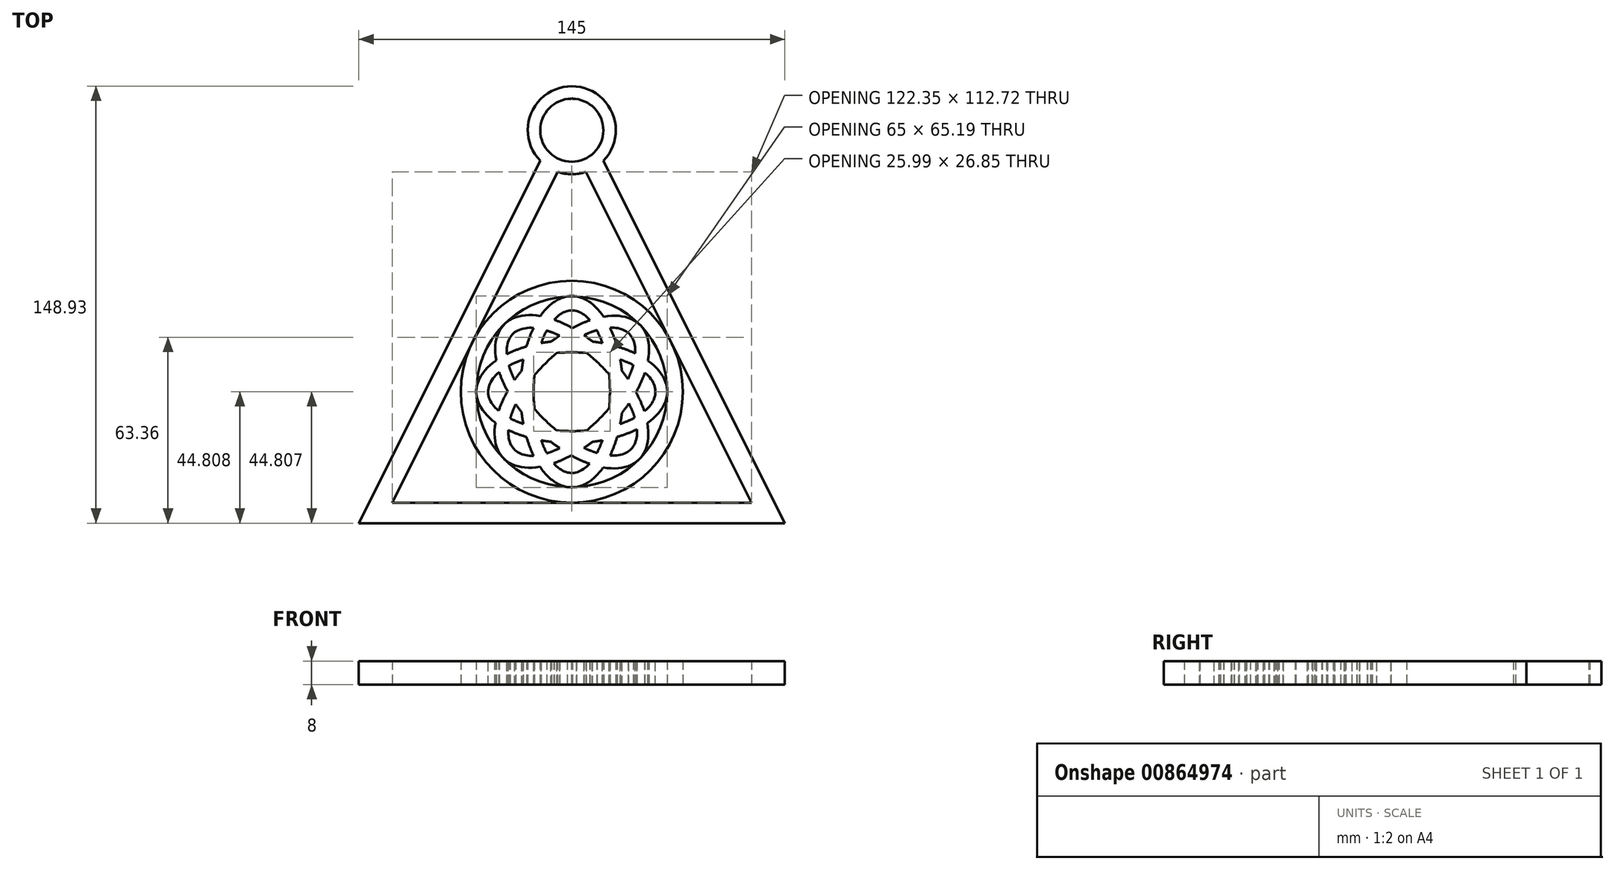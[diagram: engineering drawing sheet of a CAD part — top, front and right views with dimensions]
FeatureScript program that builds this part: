
annotation { "Feature Type Name" : "Feature", "Feature Type Description" : "" }
export const myFeature = defineFeature(function(context is Context, id is Id, definition is map)
    precondition{}
    {
        {
            var Q0;
            Q0=qCreatedBy(makeId("Top.planeOp"),FACE);
            var sketch = newSketch(context, id + "F0", { "sketchPlane" : qUnion([Q0])});
            skLineSegment(sketch, "E0.bottom", {"start": v(72.5, -72.5) * mm, "end": v(-72.5, -72.5) * mm});
            skPoint(sketch, "E0.middle", {"position": v(0, 0) * mm});
            skLineSegment(sketch, "E1", {"start": v(0, 72.5) * mm, "end": v(-0.16, 72.18) * mm});
            skLineSegment(sketch, "E2", {"start": v(0, 72.5) * mm, "end": v(0.16, 72.18) * mm});
            skCircle(sketch, "E3", {"center": v(0, 61.43) * mm, "radius": 10.75 * mm});
            skLineSegment(sketch, "E4", {"start": v(-4.81, 47.22) * mm, "end": v(-61.17, -65.5) * mm});
            skLineSegment(sketch, "E5", {"start": v(4.81, 47.22) * mm, "end": v(61.17, -65.5) * mm});
            skLineSegment(sketch, "E6", {"start": v(-61.17, -65.5) * mm, "end": v(61.17, -65.5) * mm});
            skArc(sketch, "E7", {"start": v(-4.81, 47.22) * mm, "mid": v(0, 46.43) * mm, "end": v(4.81, 47.22) * mm});
            skLineSegment(sketch, "E8.trimOffspring", {"start": v(-10.76, 50.98) * mm, "end": v(-72.5, -72.5) * mm});
            skLineSegment(sketch, "E9.trimOffspring", {"start": v(10.76, 50.98) * mm, "end": v(72.5, -72.5) * mm});
            skArc(sketch, "E10.trimOffspring", {"start": v(10.76, 50.98) * mm, "mid": v(0, 76.43) * mm, "end": v(-10.76, 50.98) * mm});
            skCircle(sketch, "E11", {"center": v(0, -27.7) * mm, "radius": 37.8 * mm});
            skCircle(sketch, "E12", {"center": v(0, -27.7) * mm, "radius": 32.5 * mm});
            skPoint(sketch, "E0.right.end.orphan", {"position": v(-72.5, 72.5) * mm});
            skPoint(sketch, "E0.left.end.orphan", {"position": v(72.5, 72.5) * mm});
            skLineSegment(sketch, "E13", {"start": v(22.98, -4.72) * mm, "end": v(22.98, -4.71) * mm});
            skLineSegment(sketch, "E14", {"start": v(0, -27.7) * mm, "end": v(0, -27.7) * mm});
            skEllipticalArc(sketch, "E15", {});
            skEllipticalArc(sketch, "E16", {});
            skEllipticalArc(sketch, "E17", {});
            skEllipticalArc(sketch, "E18", {});
            skEllipticalArc(sketch, "E19", {});
            skEllipticalArc(sketch, "E20", {});
            skLineSegment(sketch, "E21.trimOffspring", {"start": v(-22.98, -50.67) * mm, "end": v(-22.98, -50.67) * mm});
            skLineSegment(sketch, "E22.trimOffspring", {"start": v(26.73, -0.96) * mm, "end": v(28.18, 0.49) * mm});
            skEllipticalArc(sketch, "E23.trimOffspring", {});
            skEllipticalArc(sketch, "E24.trimOffspring", {});
            skEllipticalArc(sketch, "E25.trimOffspring", {});
            skEllipticalArc(sketch, "E26.trimOffspring", {});
            skEllipticalArc(sketch, "E27.trimOffspring", {});
            skEllipticalArc(sketch, "E28.trimOffspring", {});
            skEllipticalArc(sketch, "E29.trimOffspring", {});
            skEllipticalArc(sketch, "E30.trimOffspring", {});
            skEllipticalArc(sketch, "E31.trimOffspring", {});
            skEllipticalArc(sketch, "E32.trimOffspring", {});
            skEllipticalArc(sketch, "E33.trimOffspring", {});
            skEllipticalArc(sketch, "E34.trimOffspring", {});
            skEllipticalArc(sketch, "E35.trimOffspring", {});
            skEllipticalArc(sketch, "E36.trimOffspring", {});
            skEllipticalArc(sketch, "E37.trimOffspring", {});
            skEllipticalArc(sketch, "E38.trimOffspring", {});
            skEllipticalArc(sketch, "E39.trimOffspring", {});
            skEllipticalArc(sketch, "E40.trimOffspring", {});
            skEllipticalArc(sketch, "E41.trimOffspring", {});
            skEllipticalArc(sketch, "E42.trimOffspring", {});
            skEllipticalArc(sketch, "E43.trimOffspring", {});
            skEllipticalArc(sketch, "E44.trimOffspring", {});
            skEllipticalArc(sketch, "E45.trimOffspring", {});
            skEllipticalArc(sketch, "E46.trimOffspring", {});
            skEllipticalArc(sketch, "E47.trimOffspring", {});
            skEllipticalArc(sketch, "E48.trimOffspring", {});
            skEllipticalArc(sketch, "E49.trimOffspring", {});
            skEllipticalArc(sketch, "E50.trimOffspring", {});
            skEllipticalArc(sketch, "E51.trimOffspring", {});
            skEllipticalArc(sketch, "E52.trimOffspring", {});
            skEllipticalArc(sketch, "E53.trimOffspring", {});
            skEllipticalArc(sketch, "E54", {});
            skEllipticalArc(sketch, "E55", {});
            skEllipticalArc(sketch, "E56.trimOffspring", {});
            skEllipticalArc(sketch, "E57.trimOffspring", {});
            skEllipticalArc(sketch, "E58.trimOffspring", {});
            skEllipticalArc(sketch, "E59.trimOffspring", {});
            skEllipticalArc(sketch, "E60.trimOffspring", {});
            skEllipticalArc(sketch, "E61.trimOffspring", {});
            skEllipticalArc(sketch, "E62.trimOffspring", {});
            skEllipticalArc(sketch, "E63.trimOffspring", {});
            skEllipticalArc(sketch, "E64.trimOffspring", {});
            skEllipticalArc(sketch, "E65.trimOffspring", {});
            skEllipticalArc(sketch, "E66.trimOffspring", {});
            skEllipticalArc(sketch, "E67.trimOffspring", {});
            skEllipticalArc(sketch, "E68.trimOffspring", {});
            skEllipticalArc(sketch, "E69.trimOffspring", {});
            skEllipticalArc(sketch, "E70.trimOffspring", {});
            skEllipticalArc(sketch, "E71.trimOffspring", {});
            skEllipticalArc(sketch, "E72.trimOffspring", {});
            skEllipticalArc(sketch, "E73.trimOffspring", {});
            skEllipticalArc(sketch, "E74.trimOffspring", {});
            const initialGuessF0  = {"E15": [0, -0.02769253581563259, -0.7056259441974503, 0.7085845234518298, 0.0325, 0.0175, 0.8202593312497778, 1.0718901896612705], "E16": [0, -0.02769253581563259, 0.7168995723775058, 0.697176450495102, 0.0325, 0.0175, 4.387621422207099, 5.06260565640085], "E17": [0, -0.02769253581563262, 1, 0, 0.0325, 0.0175, 2.4844537285898483, 3.7877283074279355], "E18": [0, -0.02769253581563259, 0.7172971573649525, -0.6967673844520555, 0.02811046229752428, 0.01329609070270662, 3.840370788440827, 4.074118567902202], "E19": [0, -0.02769253581563259, -1, 0, 0.028478752821683884, 0.01342728669359196, 5.762838051014843, 0.5070164903407309], "E20": [0, -0.02769253581563262, 0.7017134314980431, 0.7124593041397109, 0.02775496521845518, 0.013180611028578912, 4.265893021590639, 4.8927375753415525], "E23.trimOffspring": [0, -0.02769253581563259, 0.7168995723775058, 0.697176450495102, 0.0325, 0.0175, 1.5944196522230074, 1.9210130028110568], "E24.trimOffspring": [0, -0.02769253581563262, 0.7017134314980431, 0.7124593041397109, 0.02775496521845518, 0.013180611028578912, 1.358220444415318, 1.751144921751765], "E25.trimOffspring": [0, -0.02769253581563259, -1, 0, 0.028478752821683884, 0.01342728669359196, 5.176486248379568, 5.5624858596745845], "E26.trimOffspring": [0, -0.02769253581563262, 1, 0, 0.0325, 0.0175, 1.7860600434093978, 1.8968410911580582], "E27.trimOffspring": [0, -0.02769253581563259, -0.7056259441974503, 0.7085845234518298, 0.0325, 0.0175, 5.201397873484865, 5.4409490789096076], "E28.trimOffspring": [0, -0.02769253581563259, 0.7172971573649525, -0.6967673844520555, 0.02811046229752428, 0.01329609070270662, 2.188619455975548, 2.3967729655413517], "E29.trimOffspring": [0, -0.02769253581563262, 1, 0, 0.0325, 0.0175, 0.843702473839091, 1.0763617980398463], "E30.trimOffspring": [0, -0.02769253581563259, -1, 0, 0.028478752821683884, 0.01342728669359196, 3.8868511386471596, 4.095155283164662], "E31.trimOffspring": [0, -0.02769253581563259, -0.7056259441974503, 0.7085845234518298, 0.0325, 0.0175, 4.385052940859669, 4.697753255745525], "E32.trimOffspring": [0, -0.02769253581563262, 0.7017134314980431, 0.7124593041397109, 0.02775496521845518, 0.013180611028578912, 5.347618576639801, 5.580161312354519], "E33.trimOffspring": [0, -0.02769253581563259, 0.7172971573649525, -0.6967673844520555, 0.02811046229752428, 0.01329609070270662, 1.3923413554126483, 1.7691217892681943], "E34.trimOffspring": [0, -0.02769253581563259, 0.7168995723775058, 0.697176450495102, 0.0325, 0.0175, 5.211295117518317, 5.472539239655454], "E35.trimOffspring": [0, -0.02769253581563259, 0.7168995723775058, 0.697176450495102, 0.0325, 0.0175, 1.2460287686173048, 1.3555326101804006], "E36.trimOffspring": [0, -0.02769253581563262, 0.7017134314980431, 0.7124593041397109, 0.02775496521845518, 0.013180611028578912, 1.0788125144724194, 1.1243003680008445], "E37.trimOffspring": [0, -0.02769253581563259, -0.7056259441974503, 0.7085845234518298, 0.0325, 0.0175, 4.932464038811397, 5.04837306316837], "E38.trimOffspring": [0, -0.02769253581563259, -0.7056259441974503, 0.7085845234518298, 0.0325, 0.0175, 2.059805219895072, 2.299356425319814], "E39.trimOffspring": [0, -0.02769253581563259, 0.7172971573649525, -0.6967673844520555, 0.02811046229752428, 0.01329609070270662, 5.330212109565341, 5.5383656191311434], "E40.trimOffspring": [0, -0.02769253581563259, -1, 0, 0.028478752821683884, 0.01342728669359196, 0.7452584850573691, 2.420893206084792], "E41.trimOffspring": [0, -0.02769253581563262, 1, 0, 0.0325, 0.0175, 3.985295127428884, 5.462330338734585], "E42.trimOffspring": [0, -0.02769253581563259, -0.7056259441974503, 0.7085845234518298, 0.0325, 0.0175, 1.2434602872698783, 1.90678040957858], "E43.trimOffspring": [0, -0.02769253581563259, 0.7172971573649525, -0.6967673844520555, 0.02811046229752428, 0.01329609070270662, 4.533934009002442, 5.145789686684032], "E44.trimOffspring": [0, -0.02769253581563259, 0.7168995723775058, 0.697176450495102, 0.0325, 0.0175, 2.0697024639285235, 2.330946586065661], "E45.trimOffspring": [0, -0.02769253581563262, 0.7017134314980431, 0.7124593041397109, 0.02775496521845518, 0.013180611028578912, 2.2060259230500083, 2.438568658764724], "E46.trimOffspring": [0, -0.02769253581563259, 0.7168995723775058, 0.697176450495102, 0.0325, 0.0175, 2.4954569997516476, 3.8048967681772803], "E47.trimOffspring": [0, -0.02769253581563262, 0.7017134314980431, 0.7124593041397109, 0.02775496521845518, 0.013180611028578912, 2.6504330757497105, 3.6178718332416255], "E48.trimOffspring": [0, -0.02769253581563259, -1, 0, 0.028478752821683884, 0.01342728669359196, 2.6212453974250502, 3.648609143930524], "E49.trimOffspring": [0, -0.02769253581563262, 1, 0, 0.0325, 0.0175, 5.62604638217964, 0.6461356538381464], "E50.trimOffspring": [0, -0.02769253581563259, 0.7172971573649525, -0.6967673844520555, 0.02811046229752428, 0.01329609070270662, 0.6987781348510357, 0.9325259143124112], "E51.trimOffspring": [0, -0.02769253581563259, -0.7056259441974503, 0.7085845234518298, 0.0325, 0.0175, 3.9618519848395706, 4.2134828432510645], "E52.trimOffspring": [0, -0.02769253581563262, 0.7017134314980431, 0.7124593041397109, 0.02775496521845518, 0.013180611028578912, 5.792025729339503, 0.47627917965183647], "E53.trimOffspring": [0, -0.02769253581563259, 0.7168995723775058, 0.697176450495102, 0.0325, 0.0175, 5.637049653341441, 0.6633041145874873], "E54": [0, -0.02769253581563259, 0, 1, 0.03259452238479878, 0.0175, 0.840353569106359, 2.303999657265877], "E55": [0, -0.02769253581563259, 0, 1, 0.02769253581563259, 0.012995673164462014, 0.7175061476129648, 2.4301915206476212], "E56.trimOffspring": [0, -0.02769253581563259, 0, 1, 0.03259452238479878, 0.0175, 5.614681179315066, 0.6576390358824006], "E57.trimOffspring": [0, -0.02769253581563259, 0, 1, 0.02769253581563259, 0.012995673164462014, 5.78806487363873, 0.48132190261423563], "E58.trimOffspring": [0, -0.02769253581563259, -0.7056259441974503, 0.7085845234518298, 0.0325, 0.0175, 5.6308648753412776, 0.6571389249999476], "E59.trimOffspring": [0, -0.02769253581563259, 0.7172971573649525, -0.6967673844520555, 0.02811046229752428, 0.01329609070270662, 2.629383674220055, 3.63091425402825], "E60.trimOffspring": [0, -0.02769253581563259, 0.7168995723775058, 0.697176450495102, 0.0325, 0.0175, 0.8514204241668502, 1.0817874336947213], "E61.trimOffspring": [0, -0.02769253581563262, 0.7017134314980431, 0.7124593041397109, 0.02775496521845518, 0.013180611028578912, 0.7182569929598532, 0.928574079814909], "E62.trimOffspring": [0, -0.02769253581563259, -0.7056259441974503, 0.7085845234518298, 0.0325, 0.0175, 2.489272221751484, 3.798731578589737], "E63.trimOffspring": [0, -0.02769253581563259, 0.7172971573649525, -0.6967673844520555, 0.02811046229752428, 0.01329609070270662, 5.770976327809849, 0.4893216004384523], "E64.trimOffspring": [0, -0.02769253581563259, 0, 1, 0.02769253581563259, 0.012995673164462014, 3.8590988012027565, 5.1706711453454], "E65.trimOffspring": [0, -0.02769253581563259, 0, 1, 0.03259452238479878, 0.0175, 3.98194622269615, 5.054989284846367], "E66.trimOffspring": [0, -0.02769253581563262, 0.7017134314980431, 0.7124593041397109, 0.02775496521845518, 0.013180611028578912, 3.859849646549644, 4.070166733404703], "E67.trimOffspring": [0, -0.02769253581563259, 0, 1, 0.03259452238479878, 0.0175, 2.473088525725273, 3.7992316894721925], "E68.trimOffspring": [0, -0.02769253581563259, 0, 1, 0.02769253581563259, 0.012995673164462014, 2.6464722200489366, 3.622914556204028], "E69.trimOffspring": [0, -0.02769253581563259, 0.7168995723775058, 0.697176450495102, 0.0325, 0.0175, 3.993013077756643, 4.223380087284514], "E70.trimOffspring": [0, -0.02769253581563262, 1, 0, 0.0325, 0.0175, 1.2447515624317376, 1.6037409899389612], "E71.trimOffspring": [0, -0.02769253581563259, 0, 1, 0.02769253581563259, 0.012995673164462014, 5.354199329497341, 5.571784174237411], "E72.trimOffspring": [0, -0.02769253581563259, 0, 1, 0.03259452238479878, 0.0175, 5.204626981963693, 5.445592310855668], "E73.trimOffspring": [0, -0.02769253581563259, -1, 0, 0.028478752821683884, 0.01342728669359196, 4.248802517849333, 4.891379356791889], "E74.trimOffspring": [0, -0.02769253581563262, 1, 0, 0.0325, 0.0175, 2.0652308555499492, 2.3207376851447945]};
            skSetInitialGuess(sketch, initialGuessF0);
            skSolve(sketch);
        }
        {
            var Q0;
            Q0=makeQuery(id+"F0.imprint","IMPRINT",FACE,{"disambiguationData":[TD([[makeQuery(id+"F0.imprint","IMPRINT",EDGE,{"derivedFrom":sQuery(id+"F0.wireOp",EDGE,"E0.bottom")}),-1.0]])]});
            var Q1;
            {var subQ13=sQuery(id+"F0.wireOp",EDGE,"E11");var subQ14=makeQuery(id+"F0.imprint","INTERSECT",VERTEX,{"derivedFrom":[subQ13,sQuery(id+"F0.wireOp",EDGE,"E22.trimOffspring")]});Q1=makeQuery(id+"F0.imprint","IMPRINT",FACE,{"disambiguationData":[TD([[makeQuery(id+"F0.imprint","IMPRINT",EDGE,{"disambiguationData":[TD([[subQ14,1.0]])],"derivedFrom":subQ13}),1.0]])]});}
            var Q2;
            Q2=makeQuery(id+"F0.imprint","IMPRINT",FACE,{"disambiguationData":[TD([[makeQuery(id+"F0.imprint","IMPRINT",EDGE,{"derivedFrom":sQuery(id+"F0.wireOp",EDGE,"E15")}),1.0]])]});
            var Q3;
            {var subQ1=sQuery(id+"F0.wireOp",EDGE,"E40.trimOffspring");var subQ5=sQuery(id+"F0.wireOp",EDGE,"E54");var subQ9=makeQuery(id+"F0.imprint","INTERSECT",VERTEX,{"derivedFrom":[subQ1,subQ5]});Q3=makeQuery(id+"F0.imprint","IMPRINT",FACE,{"disambiguationData":[TD([[makeQuery(id+"F0.imprint","IMPRINT",EDGE,{"disambiguationData":[TD([[subQ9,-1.0]])],"derivedFrom":subQ1}),-1.0]])]});}
            var Q4;
            {var subQ0=sQuery(id+"F0.wireOp",EDGE,"E55");var subQ1=sQuery(id+"F0.wireOp",EDGE,"E40.trimOffspring");var subQ2=makeQuery(id+"F0.imprint","INTERSECT",VERTEX,{"derivedFrom":[subQ1,subQ0]});Q4=makeQuery(id+"F0.imprint","IMPRINT",FACE,{"disambiguationData":[TD([[makeQuery(id+"F0.imprint","IMPRINT",EDGE,{"disambiguationData":[TD([[subQ2,-1.0]])],"derivedFrom":subQ1}),1.0]])]});}
            var Q5;
            {var subQ10=sQuery(id+"F0.wireOp",EDGE,"E41.trimOffspring");var subQ11=sQuery(id+"F0.wireOp",EDGE,"E16");var subQ12=makeQuery(id+"F0.imprint","INTERSECT",VERTEX,{"derivedFrom":[subQ11,subQ10]});Q5=makeQuery(id+"F0.imprint","IMPRINT",FACE,{"disambiguationData":[TD([[makeQuery(id+"F0.imprint","IMPRINT",EDGE,{"disambiguationData":[TD([[subQ12,-1.0]])],"derivedFrom":subQ11}),1.0]])]});}
            var Q6;
            {var subQ2=sQuery(id+"F0.wireOp",EDGE,"E40.trimOffspring");var subQ9=sQuery(id+"F0.wireOp",EDGE,"E16");var subQ10=makeQuery(id+"F0.imprint","INTERSECT",VERTEX,{"derivedFrom":[subQ9,subQ2]});Q6=makeQuery(id+"F0.imprint","IMPRINT",FACE,{"disambiguationData":[TD([[makeQuery(id+"F0.imprint","IMPRINT",EDGE,{"disambiguationData":[TD([[subQ10,-1.0]])],"derivedFrom":subQ9}),1.0]])]});}
            var Q7;
            {var subQ0=sQuery(id+"F0.wireOp",EDGE,"E64.trimOffspring");var subQ1=sQuery(id+"F0.wireOp",EDGE,"E20");var subQ2=makeQuery(id+"F0.imprint","INTERSECT",VERTEX,{"derivedFrom":[subQ1,subQ0]});Q7=makeQuery(id+"F0.imprint","IMPRINT",FACE,{"disambiguationData":[TD([[makeQuery(id+"F0.imprint","IMPRINT",EDGE,{"disambiguationData":[TD([[subQ2,1.0]])],"derivedFrom":subQ1}),-1.0]])]});}
            var Q8;
            {var subQ3=sQuery(id+"F0.wireOp",EDGE,"E64.trimOffspring");var subQ5=sQuery(id+"F0.wireOp",EDGE,"E16");var subQ6=makeQuery(id+"F0.imprint","INTERSECT",VERTEX,{"derivedFrom":[subQ5,subQ3]});Q8=makeQuery(id+"F0.imprint","IMPRINT",FACE,{"disambiguationData":[TD([[makeQuery(id+"F0.imprint","IMPRINT",EDGE,{"disambiguationData":[TD([[subQ6,-1.0]])],"derivedFrom":subQ5}),-1.0]])]});}
            var Q9;
            {var subQ0=sQuery(id+"F0.wireOp",EDGE,"E42.trimOffspring");var subQ1=sQuery(id+"F0.wireOp",EDGE,"E40.trimOffspring");var subQ2=makeQuery(id+"F0.imprint","INTERSECT",VERTEX,{"derivedFrom":[subQ1,subQ0]});Q9=makeQuery(id+"F0.imprint","IMPRINT",FACE,{"disambiguationData":[TD([[makeQuery(id+"F0.imprint","IMPRINT",EDGE,{"disambiguationData":[TD([[subQ2,-1.0]])],"derivedFrom":subQ1}),-1.0]])]});}
            var Q10;
            {var subQ0=sQuery(id+"F0.wireOp",EDGE,"E64.trimOffspring");var subQ1=sQuery(id+"F0.wireOp",EDGE,"E16");var subQ2=makeQuery(id+"F0.imprint","INTERSECT",VERTEX,{"derivedFrom":[subQ1,subQ0]});Q10=makeQuery(id+"F0.imprint","IMPRINT",FACE,{"disambiguationData":[TD([[makeQuery(id+"F0.imprint","IMPRINT",EDGE,{"disambiguationData":[TD([[subQ2,-1.0]])],"derivedFrom":subQ1}),1.0]])]});}
            var Q11;
            {var subQ0=sQuery(id+"F0.wireOp",EDGE,"E33.trimOffspring");Q11=makeQuery(id+"F0.imprint","IMPRINT",FACE,{"disambiguationData":[TD([[makeQuery(id+"F0.imprint","IMPRINT",EDGE,{"derivedFrom":subQ0}),-1.0]])]});}
            var Q12;
            {var subQ0=sQuery(id+"F0.wireOp",EDGE,"E43.trimOffspring");var subQ1=sQuery(id+"F0.wireOp",EDGE,"E20");var subQ2=makeQuery(id+"F0.imprint","INTERSECT",VERTEX,{"derivedFrom":[subQ1,subQ0]});Q12=makeQuery(id+"F0.imprint","IMPRINT",FACE,{"disambiguationData":[TD([[makeQuery(id+"F0.imprint","IMPRINT",EDGE,{"disambiguationData":[TD([[subQ2,-1.0]])],"derivedFrom":subQ1}),1.0]])]});}
            var Q13;
            {var subQ0=sQuery(id+"F0.wireOp",EDGE,"E54");var subQ1=sQuery(id+"F0.wireOp",EDGE,"E40.trimOffspring");var subQ2=makeQuery(id+"F0.imprint","INTERSECT",VERTEX,{"derivedFrom":[subQ1,subQ0]});Q13=makeQuery(id+"F0.imprint","IMPRINT",FACE,{"disambiguationData":[TD([[makeQuery(id+"F0.imprint","IMPRINT",EDGE,{"disambiguationData":[TD([[subQ2,-1.0]])],"derivedFrom":subQ1}),1.0]])]});}
            var Q14;
            {var subQ0=sQuery(id+"F0.wireOp",EDGE,"E55");var subQ1=sQuery(id+"F0.wireOp",EDGE,"E41.trimOffspring");var subQ2=makeQuery(id+"F0.imprint","INTERSECT",VERTEX,{"derivedFrom":[subQ1,subQ0]});Q14=makeQuery(id+"F0.imprint","IMPRINT",FACE,{"disambiguationData":[TD([[makeQuery(id+"F0.imprint","IMPRINT",EDGE,{"disambiguationData":[TD([[subQ2,-1.0]])],"derivedFrom":subQ1}),1.0]])]});}
            var Q15;
            {var subQ0=sQuery(id+"F0.wireOp",EDGE,"E41.trimOffspring");var subQ1=sQuery(id+"F0.wireOp",EDGE,"E16");var subQ2=makeQuery(id+"F0.imprint","INTERSECT",VERTEX,{"derivedFrom":[subQ1,subQ0]});Q15=makeQuery(id+"F0.imprint","IMPRINT",FACE,{"disambiguationData":[TD([[makeQuery(id+"F0.imprint","IMPRINT",EDGE,{"disambiguationData":[TD([[subQ2,-1.0]])],"derivedFrom":subQ1}),-1.0]])]});}
            var Q16;
            {var subQ0=sQuery(id+"F0.wireOp",EDGE,"E40.trimOffspring");var subQ1=sQuery(id+"F0.wireOp",EDGE,"E16");var subQ2=makeQuery(id+"F0.imprint","INTERSECT",VERTEX,{"derivedFrom":[subQ1,subQ0]});Q16=makeQuery(id+"F0.imprint","IMPRINT",FACE,{"disambiguationData":[TD([[makeQuery(id+"F0.imprint","IMPRINT",EDGE,{"disambiguationData":[TD([[subQ2,-1.0]])],"derivedFrom":subQ1}),-1.0]])]});}
            var Q17;
            {var subQ0=sQuery(id+"F0.wireOp",EDGE,"E25.trimOffspring");var subQ1=sQuery(id+"F0.wireOp",EDGE,"E23.trimOffspring");var subQ2=makeQuery(id+"F0.imprint","INTERSECT",VERTEX,{"derivedFrom":[subQ1,subQ0]});Q17=makeQuery(id+"F0.imprint","IMPRINT",FACE,{"disambiguationData":[TD([[makeQuery(id+"F0.imprint","IMPRINT",EDGE,{"disambiguationData":[TD([[subQ2,-1.0]])],"derivedFrom":subQ1}),-1.0]])]});}
            extrude(context, id + "F1", {"entities" : qUnion([Q0, Q1, Q2, Q3, Q4, Q5, Q6, Q7, Q8, Q9, Q10, Q11, Q12, Q13, Q14, Q15, Q16, Q17]), "depth" : 8 * mm, "offsetDistance" : 25 * mm});
        }
    });
